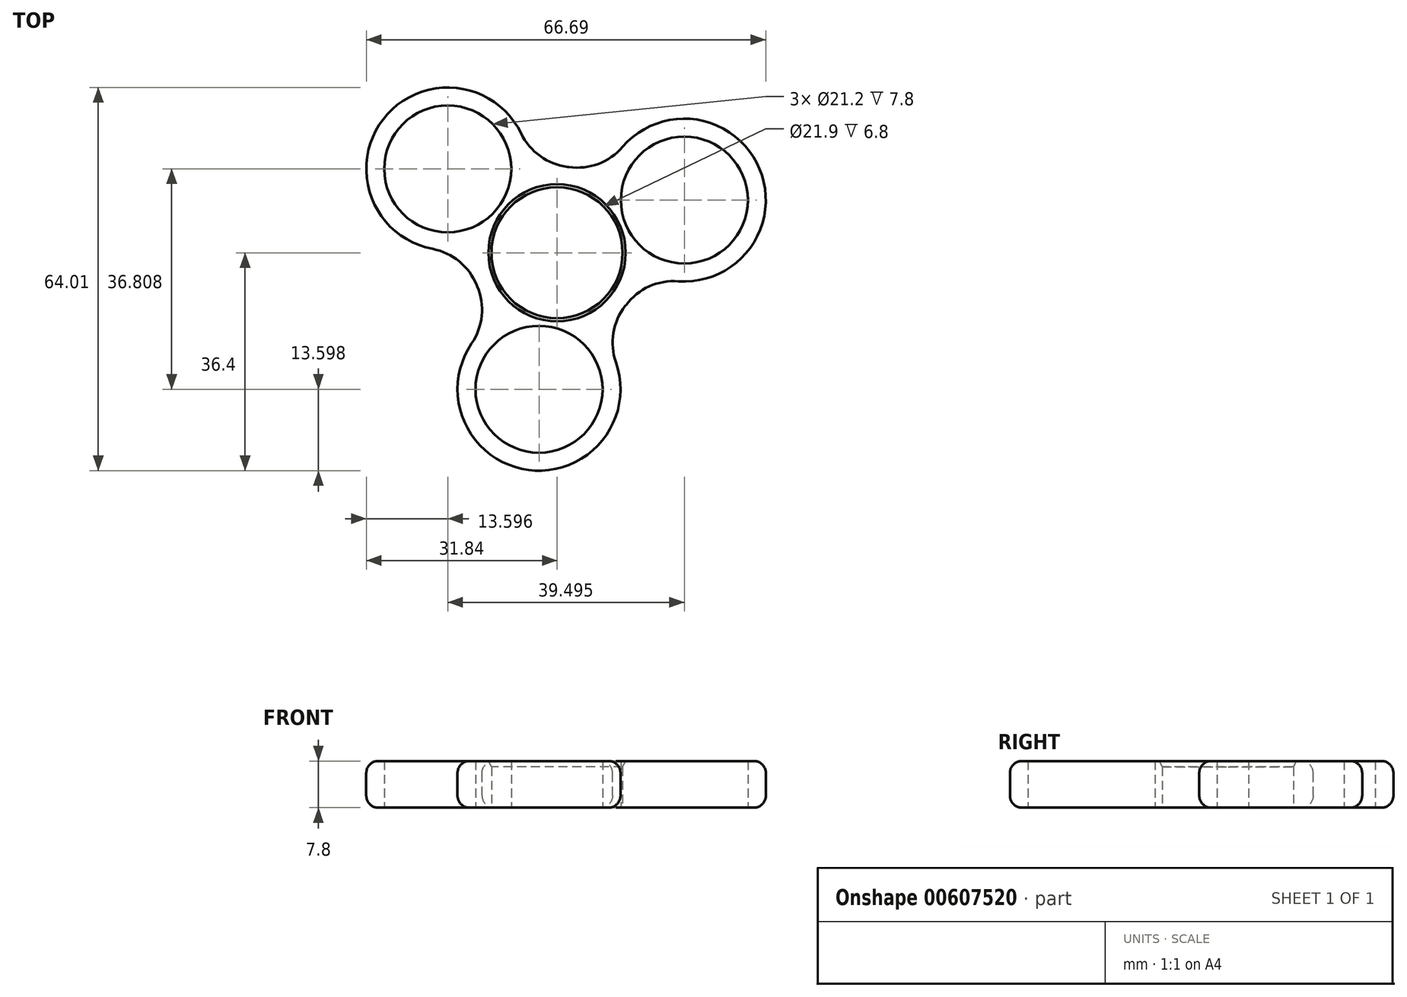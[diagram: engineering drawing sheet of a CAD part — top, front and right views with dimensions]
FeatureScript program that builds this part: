
annotation { "Feature Type Name" : "Feature", "Feature Type Description" : "" }
export const myFeature = defineFeature(function(context is Context, id is Id, definition is map)
    precondition{}
    {
        {
            var Q0;
            Q0=qCreatedBy(makeId("Top.planeOp"),FACE);
            var sketch = newSketch(context, id + "F0", { "sketchPlane" : qUnion([Q0])});
            skCircle(sketch, "E0", {"center": v(0, 0) * mm, "radius": 10.95 * mm});
            skCircle(sketch, "E1.0", {"center": v(0, 0) * mm, "radius": 14.45 * mm});
            skCircle(sketch, "E2.cCircle", {"center": v(0, 0) * mm, "radius": 11.5 * mm, "construction": true});
            skLineSegment(sketch, "E2.0", {"start": v(-18.24, 14) * mm, "end": v(21.25, 8.8) * mm, "construction": true});
            skLineSegment(sketch, "E2.1", {"start": v(21.25, 8.8) * mm, "end": v(-3, -22.8) * mm, "construction": true});
            skLineSegment(sketch, "E2.2", {"start": v(-3, -22.8) * mm, "end": v(-18.24, 14) * mm, "construction": true});
            skPoint(sketch, "E2.0.midPoint", {"position": v(1.5, 11.4) * mm});
            skCircle(sketch, "E3", {"center": v(-18.24, 14) * mm, "radius": 10.6 * mm});
            skCircle(sketch, "E4", {"center": v(21.25, 8.8) * mm, "radius": 10.6 * mm});
            skCircle(sketch, "E5", {"center": v(-3, -22.8) * mm, "radius": 10.6 * mm});
            skCircle(sketch, "E6.0", {"center": v(-18.24, 14) * mm, "radius": 13.6 * mm});
            skCircle(sketch, "E7.0", {"center": v(21.25, 8.8) * mm, "radius": 13.6 * mm});
            skCircle(sketch, "E8.0", {"center": v(-3, -22.8) * mm, "radius": 13.6 * mm});
            skSolve(sketch);
        }
        {
            var Q0;
            Q0=qSketchRegion(id+"F0",true);
            extrude(context, id + "F1", {"entities" : qUnion([Q0]), "depth" : 7.8 * mm, "offsetDistance" : 25 * mm});
        }
        {
            var Q0;
            {var subQ0=sQuery(id+"F0.wireOp",EDGE,"E6.0");var subQ1=sQuery(id+"F0.wireOp",EDGE,"E1.0");Q0=makeQuery(id+"F1.opExtrude","SWEPT_EDGE",EDGE,{"disambiguationData":[OSD([subQ1,subQ0]),TDD([makeQuery(id+"F0.imprint","INTERSECT",VERTEX,{"disambiguationData":[OD(1.0)],"derivedFrom":[subQ1,subQ0]})])]});}
            var Q1;
            {var subQ0=sQuery(id+"F0.wireOp",EDGE,"E6.0");var subQ1=sQuery(id+"F0.wireOp",EDGE,"E1.0");Q1=makeQuery(id+"F1.opExtrude","SWEPT_EDGE",EDGE,{"disambiguationData":[OSD([subQ1,subQ0]),TDD([makeQuery(id+"F0.imprint","INTERSECT",VERTEX,{"disambiguationData":[OD(0.0)],"derivedFrom":[subQ1,subQ0]})])]});}
            var Q2;
            {var subQ0=sQuery(id+"F0.wireOp",EDGE,"E7.0");var subQ1=sQuery(id+"F0.wireOp",EDGE,"E1.0");Q2=makeQuery(id+"F1.opExtrude","SWEPT_EDGE",EDGE,{"disambiguationData":[OSD([subQ1,subQ0]),TDD([makeQuery(id+"F0.imprint","INTERSECT",VERTEX,{"disambiguationData":[OD(0.0)],"derivedFrom":[subQ1,subQ0]})])]});}
            var Q3;
            {var subQ0=sQuery(id+"F0.wireOp",EDGE,"E7.0");var subQ1=sQuery(id+"F0.wireOp",EDGE,"E1.0");Q3=makeQuery(id+"F1.opExtrude","SWEPT_EDGE",EDGE,{"disambiguationData":[OSD([subQ1,subQ0]),TDD([makeQuery(id+"F0.imprint","INTERSECT",VERTEX,{"disambiguationData":[OD(1.0)],"derivedFrom":[subQ1,subQ0]})])]});}
            var Q4;
            {var subQ0=sQuery(id+"F0.wireOp",EDGE,"E8.0");var subQ1=sQuery(id+"F0.wireOp",EDGE,"E1.0");Q4=makeQuery(id+"F1.opExtrude","SWEPT_EDGE",EDGE,{"disambiguationData":[OSD([subQ1,subQ0]),TDD([makeQuery(id+"F0.imprint","INTERSECT",VERTEX,{"disambiguationData":[OD(1.0)],"derivedFrom":[subQ1,subQ0]})])]});}
            var Q5;
            {var subQ0=sQuery(id+"F0.wireOp",EDGE,"E8.0");var subQ1=sQuery(id+"F0.wireOp",EDGE,"E1.0");Q5=makeQuery(id+"F1.opExtrude","SWEPT_EDGE",EDGE,{"disambiguationData":[OSD([subQ1,subQ0]),TDD([makeQuery(id+"F0.imprint","INTERSECT",VERTEX,{"disambiguationData":[OD(0.0)],"derivedFrom":[subQ1,subQ0]})])]});}
            fillet(context, id + "F2", {"entities" : qUnion([Q0, Q1, Q2, Q3, Q4, Q5]), "radius" : 10 * mm, "tangentPropagation" : true, "allowEdgeOverflow" : false});
        }
        {
            var Q0;
            {var subQ0=sQuery(id+"F0.wireOp",EDGE,"E7.0");var subQ1=sQuery(id+"F0.wireOp",EDGE,"E1.0");Q0=makeQuery(id+"F2.opFillet","BLEND_EDGE",EDGE,{"blendedFrom":[makeQuery(id+"F1.opExtrude","SWEPT_EDGE",EDGE,{"disambiguationData":[OSD([subQ1,subQ0]),TDD([makeQuery(id+"F0.imprint","INTERSECT",VERTEX,{"disambiguationData":[OD(1.0)],"derivedFrom":[subQ1,subQ0]})])]}),makeQuery(id+"F1.opExtrude","CAP_FACE",FACE,{"disambiguationData":[OSD([sQuery(id+"F0.wireOp",EDGE,"E0"),subQ1,sQuery(id+"F0.wireOp",EDGE,"E3"),sQuery(id+"F0.wireOp",EDGE,"E4"),sQuery(id+"F0.wireOp",EDGE,"E5"),sQuery(id+"F0.wireOp",EDGE,"E6.0"),subQ0,sQuery(id+"F0.wireOp",EDGE,"E8.0")])],"isStart":true})],"blendedInto":[makeQuery(id+"F1.opExtrude","CAP_FACE",FACE,{"disambiguationData":[OSD([sQuery(id+"F0.wireOp",EDGE,"E0"),subQ1,sQuery(id+"F0.wireOp",EDGE,"E3"),sQuery(id+"F0.wireOp",EDGE,"E4"),sQuery(id+"F0.wireOp",EDGE,"E5"),sQuery(id+"F0.wireOp",EDGE,"E6.0"),subQ0,sQuery(id+"F0.wireOp",EDGE,"E8.0")])],"isStart":true})]});}
            var Q1;
            {var subQ0=sQuery(id+"F0.wireOp",EDGE,"E8.0");var subQ1=sQuery(id+"F0.wireOp",EDGE,"E1.0");Q1=makeQuery(id+"F2.opFillet","BLEND_EDGE",EDGE,{"blendedFrom":[makeQuery(id+"F1.opExtrude","SWEPT_EDGE",EDGE,{"disambiguationData":[OSD([subQ1,subQ0]),TDD([makeQuery(id+"F0.imprint","INTERSECT",VERTEX,{"disambiguationData":[OD(0.0)],"derivedFrom":[subQ1,subQ0]})])]}),makeQuery(id+"F1.opExtrude","CAP_FACE",FACE,{"disambiguationData":[OSD([sQuery(id+"F0.wireOp",EDGE,"E0"),subQ1,sQuery(id+"F0.wireOp",EDGE,"E3"),sQuery(id+"F0.wireOp",EDGE,"E4"),sQuery(id+"F0.wireOp",EDGE,"E5"),sQuery(id+"F0.wireOp",EDGE,"E6.0"),sQuery(id+"F0.wireOp",EDGE,"E7.0"),subQ0])],"isStart":false})],"blendedInto":[makeQuery(id+"F1.opExtrude","CAP_FACE",FACE,{"disambiguationData":[OSD([sQuery(id+"F0.wireOp",EDGE,"E0"),subQ1,sQuery(id+"F0.wireOp",EDGE,"E3"),sQuery(id+"F0.wireOp",EDGE,"E4"),sQuery(id+"F0.wireOp",EDGE,"E5"),sQuery(id+"F0.wireOp",EDGE,"E6.0"),sQuery(id+"F0.wireOp",EDGE,"E7.0"),subQ0])],"isStart":false})]});}
            var Q2;
            Q2=makeQuery(id+"F1.opExtrude","CAP_EDGE",EDGE,{"disambiguationData":[OSD([sQuery(id+"F0.wireOp",EDGE,"E6.0")])],"isStart":false});
            var Q3;
            Q3=makeQuery(id+"F1.opExtrude","CAP_EDGE",EDGE,{"disambiguationData":[OSD([sQuery(id+"F0.wireOp",EDGE,"E7.0")])],"isStart":false});
            var Q4;
            Q4=makeQuery(id+"F1.opExtrude","CAP_EDGE",EDGE,{"disambiguationData":[OSD([sQuery(id+"F0.wireOp",EDGE,"E8.0")])],"isStart":true});
            var Q5;
            Q5=makeQuery(id+"F1.opExtrude","CAP_EDGE",EDGE,{"disambiguationData":[OSD([sQuery(id+"F0.wireOp",EDGE,"E6.0")])],"isStart":true});
            fillet(context, id + "F3", {"entities" : qUnion([Q0, Q1, Q2, Q3, Q4, Q5]), "radius" : 2 * mm, "tangentPropagation" : true, "allowEdgeOverflow" : false});
        }
        {
            var Q0;
            Q0=makeQuery(id+"F1.opExtrude","CAP_EDGE",EDGE,{"disambiguationData":[OSD([sQuery(id+"F0.wireOp",EDGE,"E0")])],"isStart":false});
            chamfer(context, id + "F4", {"entities" : qUnion([Q0]), "chamferType" : ChamferType.TWO_OFFSETS, "width1" : 1 * mm, "oppositeDirection" : false, "width2" : .5 * mm, "tangentPropagation" : true});
        }
    });
